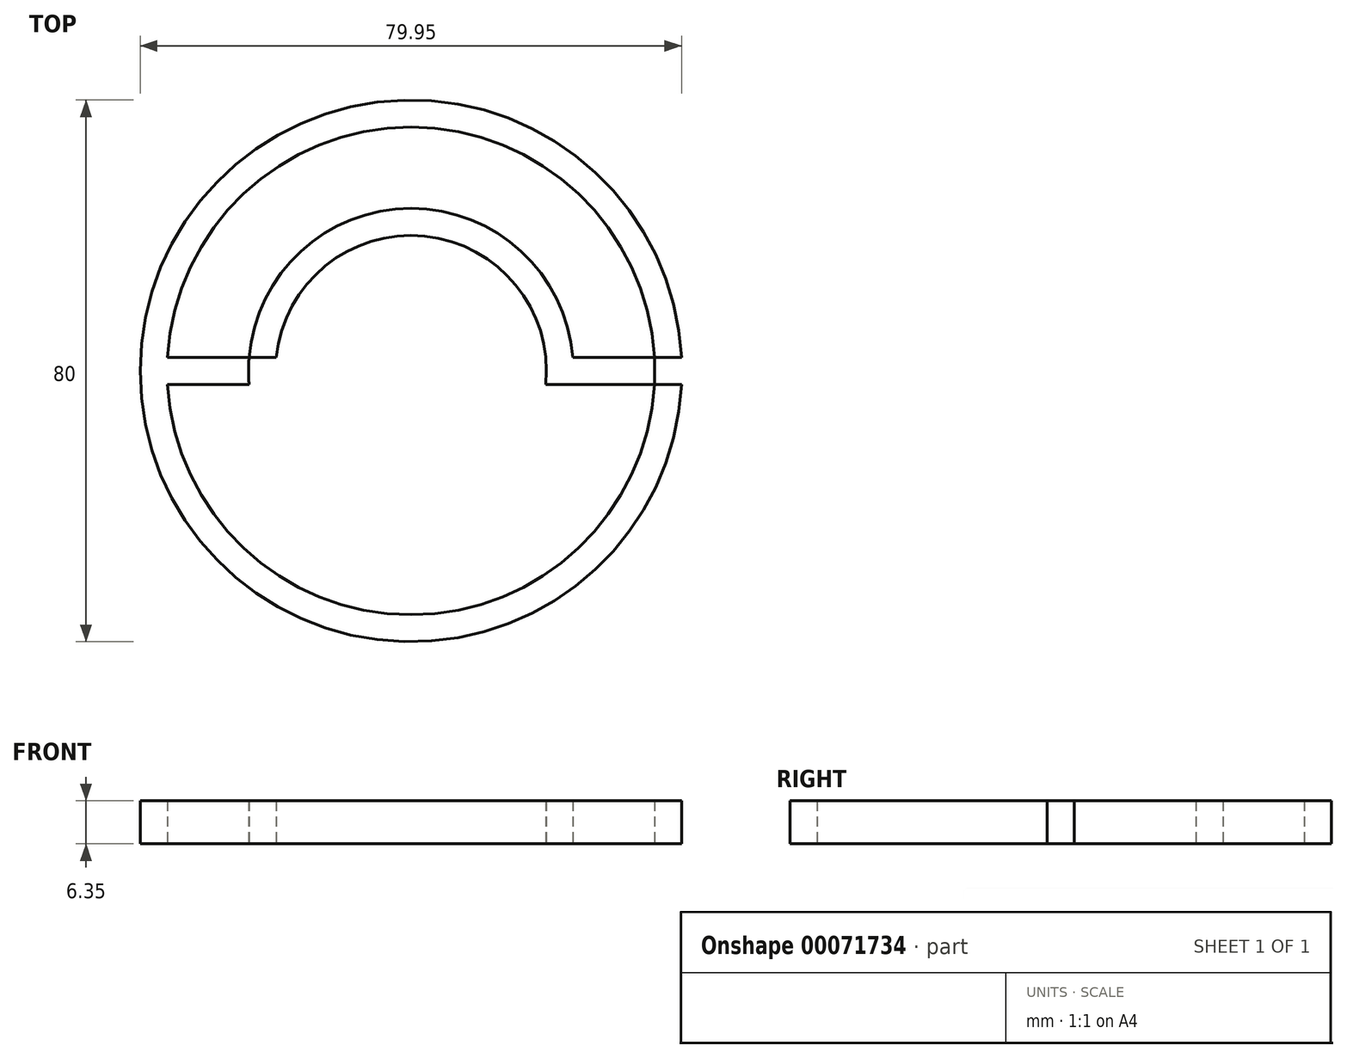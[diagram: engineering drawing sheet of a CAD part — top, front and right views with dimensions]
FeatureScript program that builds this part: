
annotation { "Feature Type Name" : "Feature", "Feature Type Description" : "" }
export const myFeature = defineFeature(function(context is Context, id is Id, definition is map)
    precondition{}
    {
        {
            var Q0;
            Q0=qCreatedBy(makeId("Top.planeOp"),FACE);
            var sketch = newSketch(context, id + "F0", { "sketchPlane" : qUnion([Q0])});
            skCircle(sketch, "E0", {"center": v(0, -1.2) * mm, "radius": 40 * mm});
            skCircle(sketch, "E1", {"center": v(0, -1.2) * mm, "radius": 36 * mm});
            skLineSegment(sketch, "E2.bottom", {"start": v(-40, -3.2) * mm, "end": v(40, -3.2) * mm});
            skLineSegment(sketch, "E2.top", {"start": v(-40, 0.8) * mm, "end": v(40, 0.8) * mm});
            skLineSegment(sketch, "E2.left", {"start": v(-40, 0.8) * mm, "end": v(-40, -3.2) * mm});
            skLineSegment(sketch, "E2.right", {"start": v(40, 0.8) * mm, "end": v(40, -3.2) * mm});
            skLineSegment(sketch, "E3", {"start": v(0, 0.8) * mm, "end": v(0, -3.2) * mm, "construction": true});
            skCircle(sketch, "E4", {"center": v(0, -1.2) * mm, "radius": 20 * mm});
            skCircle(sketch, "E5", {"center": v(0, -1.2) * mm, "radius": 24 * mm});
            skLineSegment(sketch, "E6", {"start": v(0, 18.8) * mm, "end": v(0, 22.8) * mm, "construction": true});
            skSolve(sketch);
        }
        {
            var Q0;
            {var subQ0=sQuery(id+"F0.wireOp",EDGE,"E2.top");var subQ1=sQuery(id+"F0.wireOp",EDGE,"E0");var subQ2=makeQuery(id+"F0.imprint","INTERSECT",VERTEX,{"disambiguationData":[OD(0.0)],"derivedFrom":[subQ1,subQ0]});Q0=makeQuery(id+"F0.imprint","IMPRINT",FACE,{"disambiguationData":[TD([[makeQuery(id+"F0.imprint","IMPRINT",EDGE,{"disambiguationData":[TD([[subQ2,-1.0]])],"derivedFrom":subQ1}),1.0]])]});}
            var Q1;
            {var subQ1=sQuery(id+"F0.wireOp",EDGE,"E0");var subQ5=sQuery(id+"F0.wireOp",EDGE,"E2.top");var subQ8=makeQuery(id+"F0.imprint","INTERSECT",VERTEX,{"disambiguationData":[OD(1.0)],"derivedFrom":[subQ1,subQ5]});Q1=makeQuery(id+"F0.imprint","IMPRINT",FACE,{"disambiguationData":[TD([[makeQuery(id+"F0.imprint","IMPRINT",EDGE,{"disambiguationData":[TD([[subQ8,-1.0]])],"derivedFrom":subQ1}),1.0]])]});}
            var Q2;
            {var subQ0=sQuery(id+"F0.wireOp",EDGE,"E2.bottom");var subQ1=sQuery(id+"F0.wireOp",EDGE,"E0");var subQ2=makeQuery(id+"F0.imprint","INTERSECT",VERTEX,{"disambiguationData":[OD(0.0)],"derivedFrom":[subQ1,subQ0]});Q2=makeQuery(id+"F0.imprint","IMPRINT",FACE,{"disambiguationData":[TD([[makeQuery(id+"F0.imprint","IMPRINT",EDGE,{"disambiguationData":[TD([[subQ2,-1.0]])],"derivedFrom":subQ1}),1.0]])]});}
            var Q3;
            {var subQ0=sQuery(id+"F0.wireOp",EDGE,"E2.top");var subQ5=sQuery(id+"F0.wireOp",EDGE,"E0");var subQ8=makeQuery(id+"F0.imprint","INTERSECT",VERTEX,{"disambiguationData":[OD(0.0)],"derivedFrom":[subQ5,subQ0]});Q3=makeQuery(id+"F0.imprint","IMPRINT",FACE,{"disambiguationData":[TD([[makeQuery(id+"F0.imprint","IMPRINT",EDGE,{"disambiguationData":[TD([[subQ8,1.0]])],"derivedFrom":subQ5}),1.0]])]});}
            var Q4;
            {var subQ0=sQuery(id+"F0.wireOp",EDGE,"E2.top");var subQ1=sQuery(id+"F0.wireOp",EDGE,"E1");var subQ2=makeQuery(id+"F0.imprint","INTERSECT",VERTEX,{"disambiguationData":[OD(1.0)],"derivedFrom":[subQ1,subQ0]});Q4=makeQuery(id+"F0.imprint","IMPRINT",FACE,{"disambiguationData":[TD([[makeQuery(id+"F0.imprint","IMPRINT",EDGE,{"disambiguationData":[TD([[subQ2,1.0]])],"derivedFrom":subQ1}),1.0]])]});}
            var Q5;
            {var subQ0=sQuery(id+"F0.wireOp",EDGE,"E4");var subQ1=sQuery(id+"F0.wireOp",EDGE,"E2.bottom");var subQ2=makeQuery(id+"F0.imprint","INTERSECT",VERTEX,{"disambiguationData":[OD(1.0)],"derivedFrom":[subQ1,subQ0]});Q5=makeQuery(id+"F0.imprint","IMPRINT",FACE,{"disambiguationData":[TD([[makeQuery(id+"F0.imprint","IMPRINT",EDGE,{"disambiguationData":[TD([[subQ2,-1.0]])],"derivedFrom":subQ1}),1.0]])]});}
            var Q6;
            {var subQ0=sQuery(id+"F0.wireOp",EDGE,"E5");var subQ1=sQuery(id+"F0.wireOp",EDGE,"E2.top");var subQ2=makeQuery(id+"F0.imprint","INTERSECT",VERTEX,{"disambiguationData":[OD(0.0)],"derivedFrom":[subQ1,subQ0]});Q6=makeQuery(id+"F0.imprint","IMPRINT",FACE,{"disambiguationData":[TD([[makeQuery(id+"F0.imprint","IMPRINT",EDGE,{"disambiguationData":[TD([[subQ2,-1.0]])],"derivedFrom":subQ1}),1.0]])]});}
            var Q7;
            {var subQ0=sQuery(id+"F0.wireOp",EDGE,"E5");var subQ1=sQuery(id+"F0.wireOp",EDGE,"E2.bottom");var subQ2=makeQuery(id+"F0.imprint","INTERSECT",VERTEX,{"disambiguationData":[OD(0.0)],"derivedFrom":[subQ1,subQ0]});Q7=makeQuery(id+"F0.imprint","IMPRINT",FACE,{"disambiguationData":[TD([[makeQuery(id+"F0.imprint","IMPRINT",EDGE,{"disambiguationData":[TD([[subQ2,-1.0]])],"derivedFrom":subQ1}),1.0]])]});}
            var Q8;
            {var subQ0=sQuery(id+"F0.wireOp",EDGE,"E2.top");var subQ1=sQuery(id+"F0.wireOp",EDGE,"E1");var subQ2=makeQuery(id+"F0.imprint","INTERSECT",VERTEX,{"disambiguationData":[OD(0.0)],"derivedFrom":[subQ1,subQ0]});Q8=makeQuery(id+"F0.imprint","IMPRINT",FACE,{"disambiguationData":[TD([[makeQuery(id+"F0.imprint","IMPRINT",EDGE,{"disambiguationData":[TD([[subQ2,-1.0]])],"derivedFrom":subQ1}),1.0]])]});}
            extrude(context, id + "F1", {"entities" : qUnion([Q0, Q1, Q2, Q3, Q4, Q5, Q6, Q7, Q8]), "depth" : 6.35 * mm});
        }
    });
